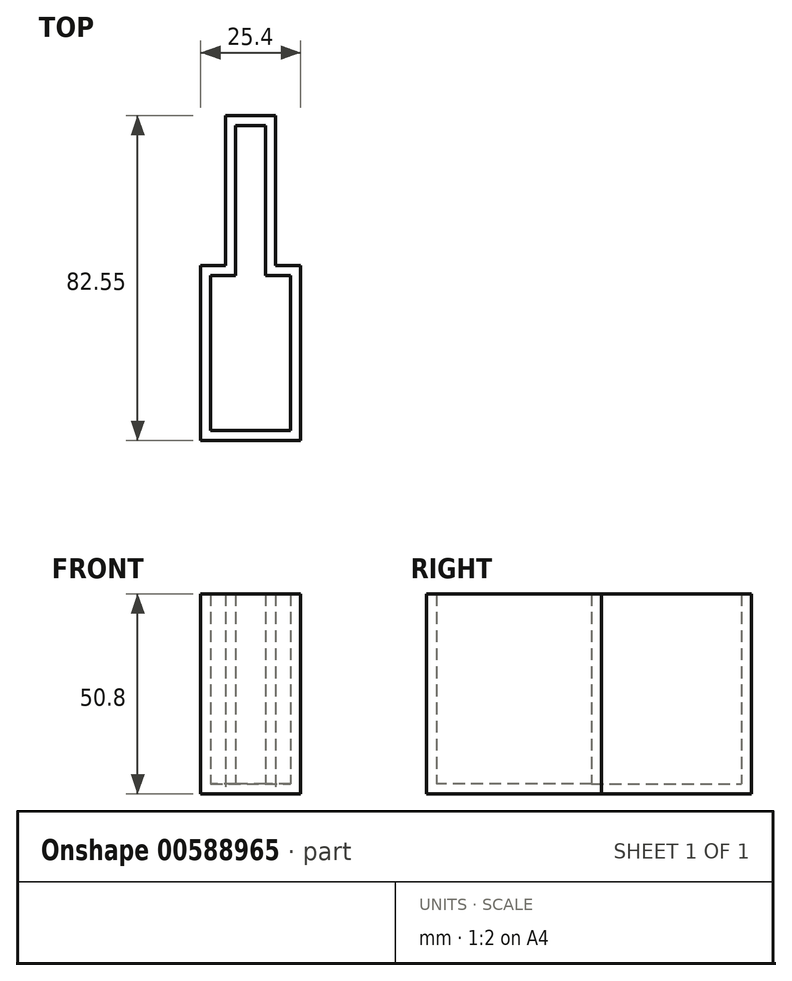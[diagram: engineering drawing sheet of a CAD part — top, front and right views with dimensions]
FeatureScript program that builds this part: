
annotation { "Feature Type Name" : "Feature", "Feature Type Description" : "" }
export const myFeature = defineFeature(function(context is Context, id is Id, definition is map)
    precondition{}
    {
        {
            var Q0;
            Q0=qCreatedBy(makeId("Top.planeOp"),FACE);
            var sketch = newSketch(context, id + "F0", { "sketchPlane" : qUnion([Q0])});
            skLineSegment(sketch, "E0", {"start": v(0, 0) * mm, "end": v(25.4, 0) * mm});
            skLineSegment(sketch, "E1", {"start": v(25.4, 0) * mm, "end": v(25.4, 44.45) * mm});
            skLineSegment(sketch, "E2", {"start": v(25.4, 44.45) * mm, "end": v(19.05, 44.45) * mm});
            skLineSegment(sketch, "E3", {"start": v(19.05, 44.45) * mm, "end": v(19.05, 82.55) * mm});
            skLineSegment(sketch, "E4", {"start": v(19.05, 82.55) * mm, "end": v(6.35, 82.55) * mm});
            skLineSegment(sketch, "E5", {"start": v(6.35, 82.55) * mm, "end": v(6.35, 44.45) * mm});
            skLineSegment(sketch, "E6", {"start": v(6.35, 44.45) * mm, "end": v(0, 44.45) * mm});
            skLineSegment(sketch, "E7", {"start": v(0, 44.45) * mm, "end": v(0, 0) * mm});
            skSolve(sketch);
        }
        {
            var Q0;
            Q0=makeQuery(id+"F0.imprint","IMPRINT",FACE,{"disambiguationData":[TD([[makeQuery(id+"F0.imprint","IMPRINT",EDGE,{"derivedFrom":sQuery(id+"F0.wireOp",EDGE,"E0")}),1.0]])]});
            extrude(context, id + "F1", {"entities" : qUnion([Q0]), "depth" : 50.8 * mm, "offsetDistance" : 25.4 * mm});
        }
        {
            var Q0;
            Q0=makeQuery(id+"F1.opExtrude","CAP_FACE",FACE,{"disambiguationData":[OSD([sQuery(id+"F0.wireOp",EDGE,"E0"),sQuery(id+"F0.wireOp",EDGE,"E1"),sQuery(id+"F0.wireOp",EDGE,"E2"),sQuery(id+"F0.wireOp",EDGE,"E3"),sQuery(id+"F0.wireOp",EDGE,"E4"),sQuery(id+"F0.wireOp",EDGE,"E5"),sQuery(id+"F0.wireOp",EDGE,"E6"),sQuery(id+"F0.wireOp",EDGE,"E7")])],"isStart":false});
            shell(context, id + "F2", {"entities" : qUnion([Q0]), "thickness" : 2.54 * mm});
        }
    });
